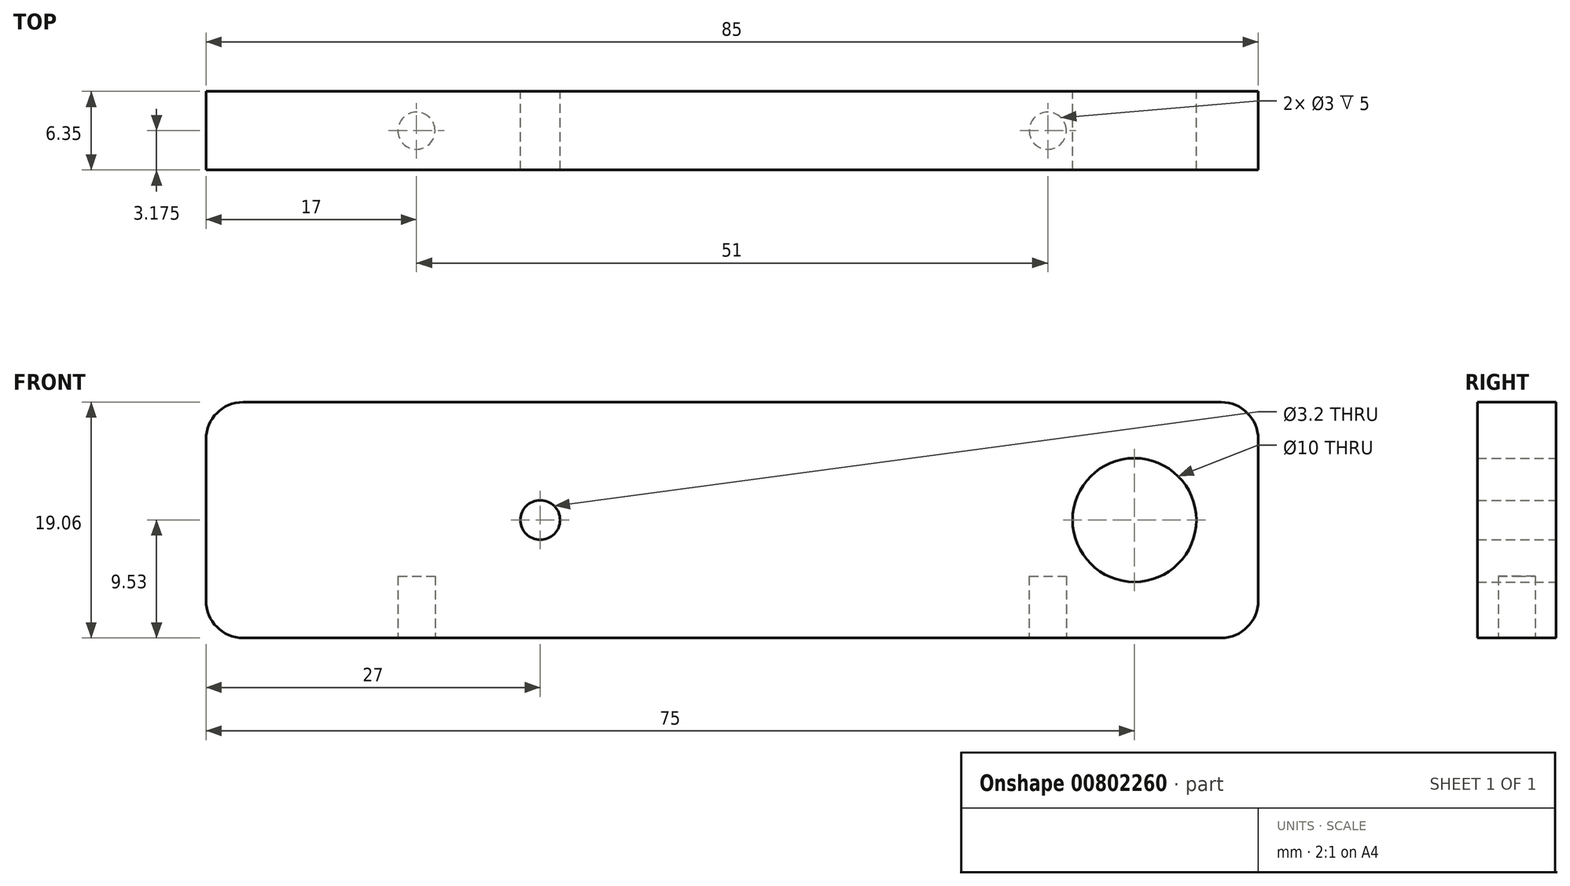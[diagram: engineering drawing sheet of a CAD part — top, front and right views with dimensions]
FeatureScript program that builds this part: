
annotation { "Feature Type Name" : "Feature", "Feature Type Description" : "" }
export const myFeature = defineFeature(function(context is Context, id is Id, definition is map)
    precondition{}
    {
        {
            var Q0;
            Q0=qCreatedBy(makeId("Front.planeOp"),FACE);
            var sketch = newSketch(context, id + "F0", { "sketchPlane" : qUnion([Q0])});
            skLineSegment(sketch, "E0.bottom", {"start": v(-42.5, 9.53) * mm, "end": v(42.5, 9.53) * mm});
            skLineSegment(sketch, "E0.top", {"start": v(-42.5, -9.53) * mm, "end": v(42.5, -9.53) * mm});
            skLineSegment(sketch, "E0.left", {"start": v(-42.5, 9.53) * mm, "end": v(-42.5, -9.53) * mm});
            skLineSegment(sketch, "E0.right", {"start": v(42.5, 9.53) * mm, "end": v(42.5, -9.53) * mm});
            skPoint(sketch, "E0.middle", {"position": v(0, 0) * mm});
            skCircle(sketch, "E1", {"center": v(-15.5, 0) * mm, "radius": 1.6 * mm});
            skCircle(sketch, "E2", {"center": v(32.5, 0) * mm, "radius": 5 * mm});
            skSolve(sketch);
        }
        {
            var Q0;
            Q0 = qSketchRegion(id + "F0", true);
            extrude(context, id + "F1", {"entities" : qUnion([Q0]), "depth" : 6.35 * mm, "offsetDistance" : 25 * mm});
        }
        {
            var Q0;
            Q0=makeQuery(id+"F1.opExtrude","SWEPT_FACE",FACE,{"disambiguationData":[OSD([sQuery(id+"F0.wireOp",EDGE,"E0.top")])]});
            var sketch = newSketch(context, id + "F2", { "sketchPlane" : qUnion([Q0])});
            skCircle(sketch, "E3", {"center": v(-25.5, 3.18) * mm, "radius": 1.5 * mm});
            skPoint(sketch, "E3.centerSnap0", {"position": v(-42.5, 3.17) * mm});
            skCircle(sketch, "E4.MirrorC", {"center": v(25.5, 3.18) * mm, "radius": 1.5 * mm});
            skSolve(sketch);
        }
        {
            var Q0;
            Q0 = qSketchRegion(id + "F2", true);
            extrude(context, id + "F3", {"entities" : qUnion([Q0]), "operationType" : NewBodyOperationType.REMOVE, "oppositeDirection" : true, "depth" : 5 * mm, "offsetDistance" : 25 * mm});
        }
        {
            var Q0;
            Q0=makeQuery(id+"F1.opExtrude","SWEPT_EDGE",EDGE,{"disambiguationData":[OSD([sQuery(id+"F0.wireOp",EDGE,"E0.bottom"),sQuery(id+"F0.wireOp",EDGE,"E0.right")])]});
            var Q1;
            Q1=makeQuery(id+"F1.opExtrude","SWEPT_EDGE",EDGE,{"disambiguationData":[OSD([sQuery(id+"F0.wireOp",EDGE,"E0.top"),sQuery(id+"F0.wireOp",EDGE,"E0.right")])]});
            var Q2;
            Q2=makeQuery(id+"F1.opExtrude","SWEPT_EDGE",EDGE,{"disambiguationData":[OSD([sQuery(id+"F0.wireOp",EDGE,"E0.top"),sQuery(id+"F0.wireOp",EDGE,"E0.left")])]});
            var Q3;
            Q3=makeQuery(id+"F1.opExtrude","SWEPT_EDGE",EDGE,{"disambiguationData":[OSD([sQuery(id+"F0.wireOp",EDGE,"E0.bottom"),sQuery(id+"F0.wireOp",EDGE,"E0.left")])]});
            fillet(context, id + "F4", {"entities" : qUnion([Q0, Q1, Q2, Q3]), "radius" : 3 * mm, "tangentPropagation" : true, "allowEdgeOverflow" : false});
        }
    });
